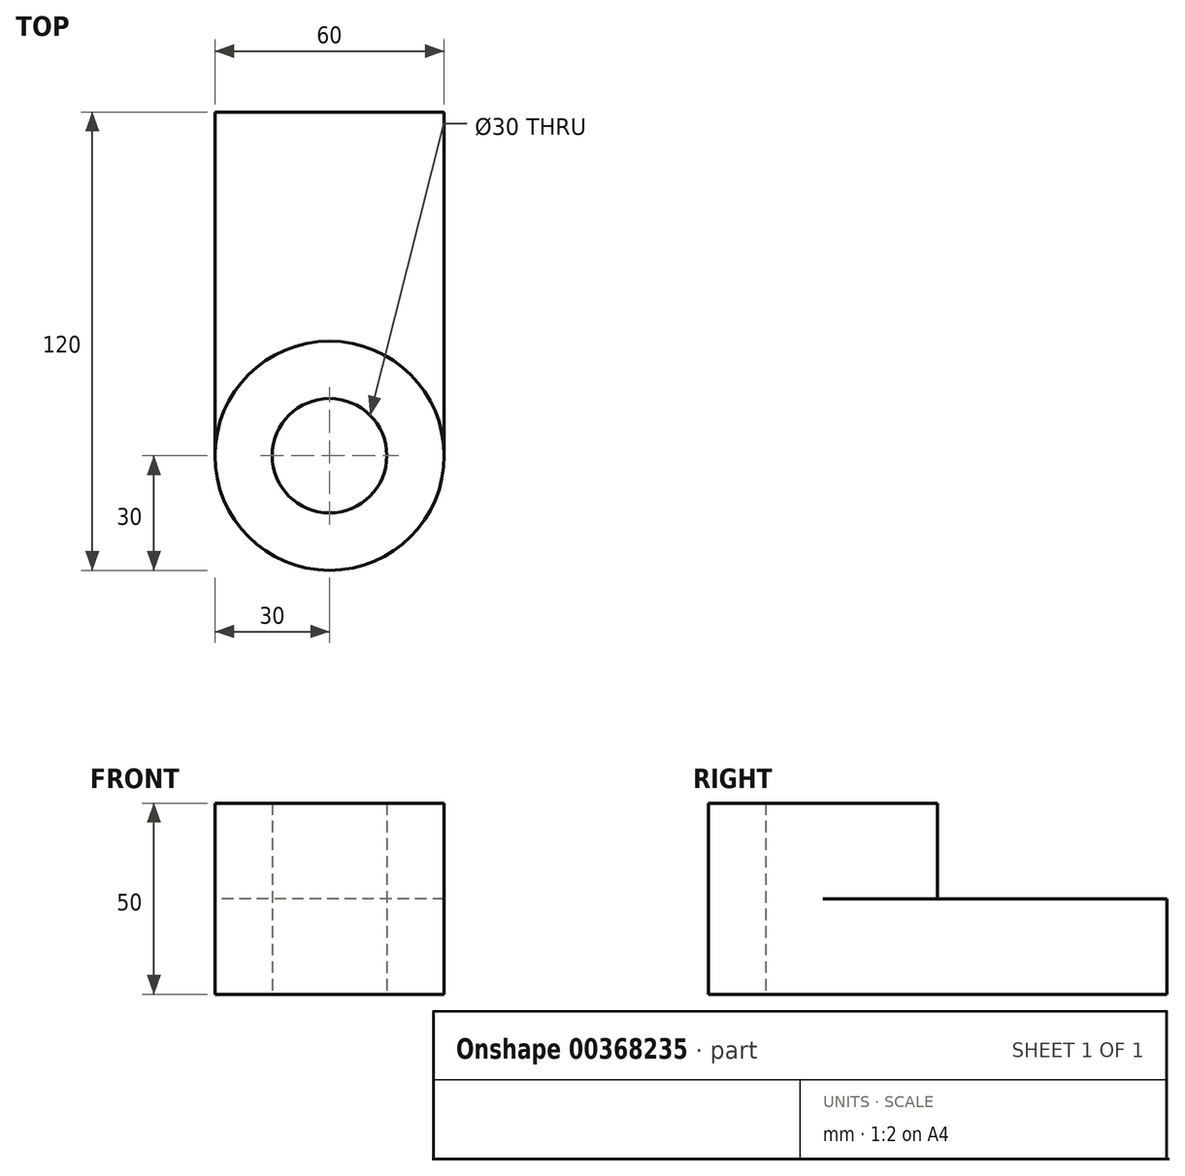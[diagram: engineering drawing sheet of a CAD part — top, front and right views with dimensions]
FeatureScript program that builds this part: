
annotation { "Feature Type Name" : "Feature", "Feature Type Description" : "" }
export const myFeature = defineFeature(function(context is Context, id is Id, definition is map)
    precondition{}
    {
        {
            var Q0;
            Q0=qCreatedBy(makeId("Top.planeOp"),FACE);
            var sketch = newSketch(context, id + "F0", { "sketchPlane" : qUnion([Q0])});
            skLineSegment(sketch, "E0.bottom", {"start": v(30, 45) * mm, "end": v(-30, 45) * mm});
            skLineSegment(sketch, "E0.left", {"start": v(30, 45) * mm, "end": v(30, -45) * mm});
            skLineSegment(sketch, "E0.right", {"start": v(-30, 45) * mm, "end": v(-30, -45) * mm});
            skPoint(sketch, "E0.middle", {"position": v(0, 0) * mm});
            skCircle(sketch, "E1", {"center": v(0, -45) * mm, "radius": 30 * mm});
            skCircle(sketch, "E2", {"center": v(0, -45) * mm, "radius": 15 * mm});
            skSolve(sketch);
        }
        {
            var Q0;
            Q0=makeQuery(id+"F0.imprint","IMPRINT",FACE,{"disambiguationData":[TD([[makeQuery(id+"F0.imprint","IMPRINT",EDGE,{"derivedFrom":sQuery(id+"F0.wireOp",EDGE,"E0.bottom")}),1.0]])]});
            var Q1;
            Q1=makeQuery(id+"F0.imprint","IMPRINT",FACE,{"disambiguationData":[TD([[makeQuery(id+"F0.imprint","IMPRINT",EDGE,{"derivedFrom":sQuery(id+"F0.wireOp",EDGE,"E2")}),-1.0]])]});
            extrude(context, id + "F1", {"entities" : qUnion([Q0, Q1]), "depth" : 25 * mm});
        }
        {
            var Q0;
            Q0=makeQuery(id+"F1.opExtrude","CAP_FACE",FACE,{"disambiguationData":[OSD([sQuery(id+"F0.wireOp",EDGE,"E0.bottom"),sQuery(id+"F0.wireOp",EDGE,"E0.left"),sQuery(id+"F0.wireOp",EDGE,"E0.right"),sQuery(id+"F0.wireOp",EDGE,"E1"),sQuery(id+"F0.wireOp",EDGE,"E2")])],"isStart":true});
            var sketch = newSketch(context, id + "F2", { "sketchPlane" : qUnion([Q0])});
            skArc(sketch, "E3", {"start": v(-30, 45) * mm, "mid": v(0, 15) * mm, "end": v(30, 45) * mm});
            skSolve(sketch);
        }
        {
            var Q0;
            Q0=makeQuery(id+"F2.imprint","IMPRINT",FACE,{"disambiguationData":[TD([[makeQuery(id+"F2.imprint","IMPRINT",EDGE,{"derivedFrom":sQuery(id+"F2.wireOp",EDGE,"E3")}),1.0]])]});
            extrude(context, id + "F3", {"entities" : qUnion([Q0]), "operationType" : NewBodyOperationType.ADD, "oppositeDirection" : true, "depth" : 50 * mm});
        }
    });
